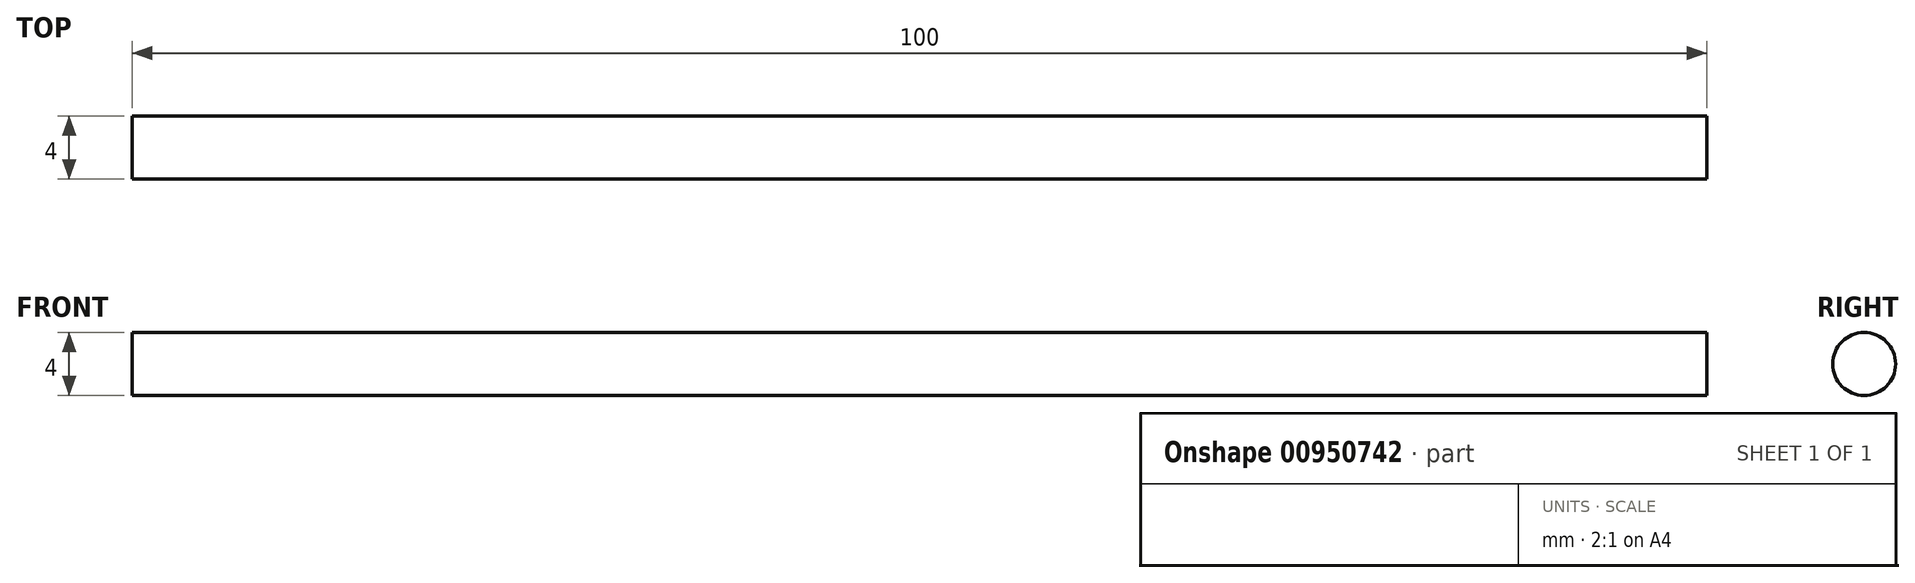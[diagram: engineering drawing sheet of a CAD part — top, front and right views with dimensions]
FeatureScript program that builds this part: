
annotation { "Feature Type Name" : "Feature", "Feature Type Description" : "" }
export const myFeature = defineFeature(function(context is Context, id is Id, definition is map)
    precondition{}
    {
        {
            var Q0;
            Q0=qCreatedBy(makeId("Front.planeOp"),FACE);
            var sketch = newSketch(context, id + "F0", { "sketchPlane" : qUnion([Q0])});
            skLineSegment(sketch, "E0", {"start": v(0, 0) * mm, "end": v(100, 0) * mm});
            skSolve(sketch);
        }
        {
            var Q0;
            Q0=qCreatedBy(makeId("Right.planeOp"),FACE);
            var sketch = newSketch(context, id + "F1", { "sketchPlane" : qUnion([Q0])});
            skCircle(sketch, "E1", {"center": v(0, 0) * mm, "radius": 2 * mm});
            skSolve(sketch);
        }
        {
            var Q0;
            Q0=makeQuery(id+"F1.imprint","IMPRINT",FACE,{"disambiguationData":[TD([[makeQuery(id+"F1.imprint","IMPRINT",EDGE,{"derivedFrom":sQuery(id+"F1.wireOp",EDGE,"E1")}),1.0]])]});
            var Q1;
            Q1=sQuery(id+"F0.wireOp",EDGE,"E0");
            sweep(context, id + "F2", {"profiles" : qUnion([Q0]), "path" : qUnion([Q1])});
        }
    });
